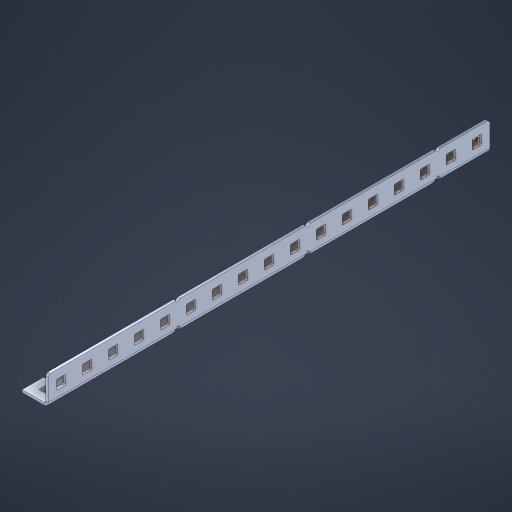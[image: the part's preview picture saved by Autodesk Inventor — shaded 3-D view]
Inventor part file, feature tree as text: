
AUTODESK INVENTOR PART (.ipt)
format: ipt  version: 2023 (Build 270158000, 158)  size: 862,208 bytes
history: native  units: in
note: dims shown in document units (in); Inventor stores cm internally (conversion verified against a paired STEP export)
features: other x58, extrude x49, sheet_metal_op x11, sketch x10, pattern_linear x2, mirror x1, chamfer x1
ambient origin geometry x8: Origin, YZ Plane, XZ Plane, XY Plane, X Axis, Y Axis, Z Axis, Center Point
bodies: Solid1 (feature_tree), Body (feature_tree)
feature tree (132):
  sheet_metal_op  "Flanges"
  other  "Flange Pattern Plane"
  other  "Flange Pattern Sketch"
  sheet_metal_op  "Flange Pattern"
  sheet_metal_op  "Body Pattern"
  pattern_linear  "Center Pattern"  Spacing1=0.0469in  [1 undecoded]
  other  "Arc Length"
  mirror  "Notch Mirror"
  pattern_linear  "Notch Pattern"  Spacing1=0.182in  [1 undecoded]
  chamfer  "End Chamfer"
  extrude  "Half Cut"  Depth=0.02in
  sketch  "Sketch1"  dims[d0=1.0in]
  other  "Plate1"
  sketch  "Sketch2"  dims[d1=8.5in]
  other  "Plate2"
  sheet_metal_op  "Bend1"
  sheet_metal_op  "Corner1"
  sketch  "Sketch3"  dims[d2=0.0469in]
  sketch  "Sketch7"  dims[d3=0.0469in]
  other  "Srf1"
  other  "Srf2"
  sketch  "Sketch8"  dims[d4=0.0234in]
  sketch  "Sketch9"  dims[d5=0.0938in]
  other  "Srf91"
  sheet_metal_op  "Body Pattern Sketch"
  other  "Srf92"
  sketch  "Sketch13"  dims[d6=0.0469in]
  sketch  "Sketch14"  dims[d7=0.5in d8=90.0deg d9=0.0312in]
  sketch  "Sketch15"  dims[d10=0.1875in]
  sketch  "Sketch16"  dims[d11=0.0469in d12=0.0469in d16=0.182in d17=0.02in d18=0.0469in d19=0.0in d20=0.25in d21=0.25in d38=6.6929in d40=0.5in d41=0.3937in d43=1.0in d46=0.172in d47=1.0in d48=0.0in d49=0.182in d50=0.02in d51=0.25in d52=0.25in d53=0.0469in d54=0.0in d55=0.172in d56=1.0in d57=0.0in d58=0.25in d60=6.6929in d62=0.5in d63=0.3937in d65=0.5in d85=0.1227in d86=0.1659in d88=0.04in d89=0.0469in d90=0.0in d91=0.04in d92=0.0491in d95=2.5in d96=0.04in d97=0.25in d98=45.0deg d99=0.25in d100=0.5in d101=0.0in d102=2.497in d106=0.182in d107=0.02in d108=0.5in d109=0.5in d110=0.0469in d111=0.0in d112=0.172in d113=0.5in d114=0.0in d117=0.5in d118=0.5in d119=0.5in]
  other  "Srf786"
  other  "Srf823"
  other  "Srf824"
  other  "Srf825"
  other  "Srf826"
  other  "Srf827"
  other  "Srf828"
  other  "Srf829"
  other  "Srf856"
  other  "Srf857"
  other  "Srf858"
  other  "Srf859"
  other  "Srf860"
  other  "Srf861"
  other  "Srf862"
  other  "Srf889"
  other  "Srf890"
  other  "Srf891"
  other  "Srf892"
  other  "Srf893"
  other  "Srf894"
  other  "Srf895"
  other  "Srf896"
  other  "Srf922"
  other  "Srf923"
  other  "Srf924"
  other  "Srf925"
  other  "Srf926"
  other  "Srf959"
  other  "Srf960"
  other  "Srf961"
  other  "Srf962"
  other  "Srf963"
  other  "Srf996"
  other  "Srf997"
  other  "Srf998"
  other  "Srf999"
  other  "Srf1000"
  other  "Srf1143"
  other  "Srf1144"
  other  "Srf1145"
  other  "Srf1199"
  other  "Srf1200"
  other  "Srf1201"
  other  "Srf1255"
  other  "Srf1256"
  other  "Srf1257"
  sheet_metal_op  "Flange Stamp"
  sheet_metal_op  "Flange Circle"
  sheet_metal_op  "Body Stamp"
  sheet_metal_op  "Body Circle"
  other  "Center Stamp"
  other  "Center Circle"
  sheet_metal_op  "Notch"
  extrude  "ExtrusionSrf2"  Depth=0.0469in
  extrude  "ExtrusionSrf92"  TaperAngle=0.0deg  [1 undecoded]
  extrude  "ExtrusionSrf823"  Depth=0.5in
  extrude  "ExtrusionSrf824"  Depth=0.5in
  extrude  "ExtrusionSrf825"  Depth=0.5in
  extrude  "ExtrusionSrf826"  Depth=0.5in
  extrude  "ExtrusionSrf827"  Depth=1.0in TaperAngle=0.0deg
  extrude  "ExtrusionSrf828"  Depth=0.182in
  extrude  "ExtrusionSrf829"  Depth=0.02in
  extrude  "ExtrusionSrf856"  Depth=0.5in
  extrude  "ExtrusionSrf857"  Depth=0.5in
  extrude  "ExtrusionSrf858"  Depth=0.0469in
  extrude  "ExtrusionSrf859"  TaperAngle=0.0deg  [1 undecoded]
  extrude  "ExtrusionSrf860"  Depth=0.5in
  extrude  "ExtrusionSrf861"  Depth=1.0in TaperAngle=0.0deg
  extrude  "ExtrusionSrf862"  Depth=0.5in
  extrude  "ExtrusionSrf889"  Depth=0.5in
  extrude  "ExtrusionSrf890"  Depth=0.5in
  extrude  "ExtrusionSrf891"  Depth=0.5in
  extrude  "ExtrusionSrf892"  Depth=0.5in
  extrude  "ExtrusionSrf893"  Depth=0.5in
  extrude  "ExtrusionSrf894"  Depth=0.0469in
  extrude  "ExtrusionSrf895"  TaperAngle=0.0deg  [1 undecoded]
  extrude  "ExtrusionSrf896"  Depth=0.5in
  extrude  "ExtrusionSrf922"  Depth=0.5in
  extrude  "ExtrusionSrf923"  Depth=0.5in
  extrude  "ExtrusionSrf924"  Depth=0.5in TaperAngle=45.0deg
  extrude  "ExtrusionSrf925"  Depth=0.5in
  extrude  "ExtrusionSrf926"  Depth=0.5in TaperAngle=0.0deg
  extrude  "ExtrusionSrf959"  Depth=0.5in
  extrude  "ExtrusionSrf960"  Depth=0.182in
  extrude  "ExtrusionSrf961"  Depth=0.02in
  extrude  "ExtrusionSrf962"  Depth=0.5in
  extrude  "ExtrusionSrf963"  Depth=0.5in
  extrude  "ExtrusionSrf996"  Depth=0.0469in
  extrude  "ExtrusionSrf997"  TaperAngle=0.0deg  [1 undecoded]
  extrude  "ExtrusionSrf998"  Depth=0.5in
  extrude  "ExtrusionSrf999"  Depth=0.5in TaperAngle=0.0deg
  extrude  "ExtrusionSrf1000"  Depth=0.5in
  extrude  "ExtrusionSrf1143"  Depth=0.5in
  extrude  "ExtrusionSrf1144"  Depth=0.5in
  extrude  "ExtrusionSrf1145"  [1 undecoded]
  extrude  "ExtrusionSrf1199"  [1 undecoded]
  extrude  "ExtrusionSrf1200"  [1 undecoded]
  extrude  "ExtrusionSrf1201"  [1 undecoded]
  extrude  "ExtrusionSrf1255"  [1 undecoded]
  extrude  "ExtrusionSrf1256"  [1 undecoded]
  extrude  "ExtrusionSrf1257"  [1 undecoded]
note: 13 required parameter values undecoded (feature->parameter linkage not recoverable at this tier; creation-order binding heuristic only, values carry confidence <= 0.55)
